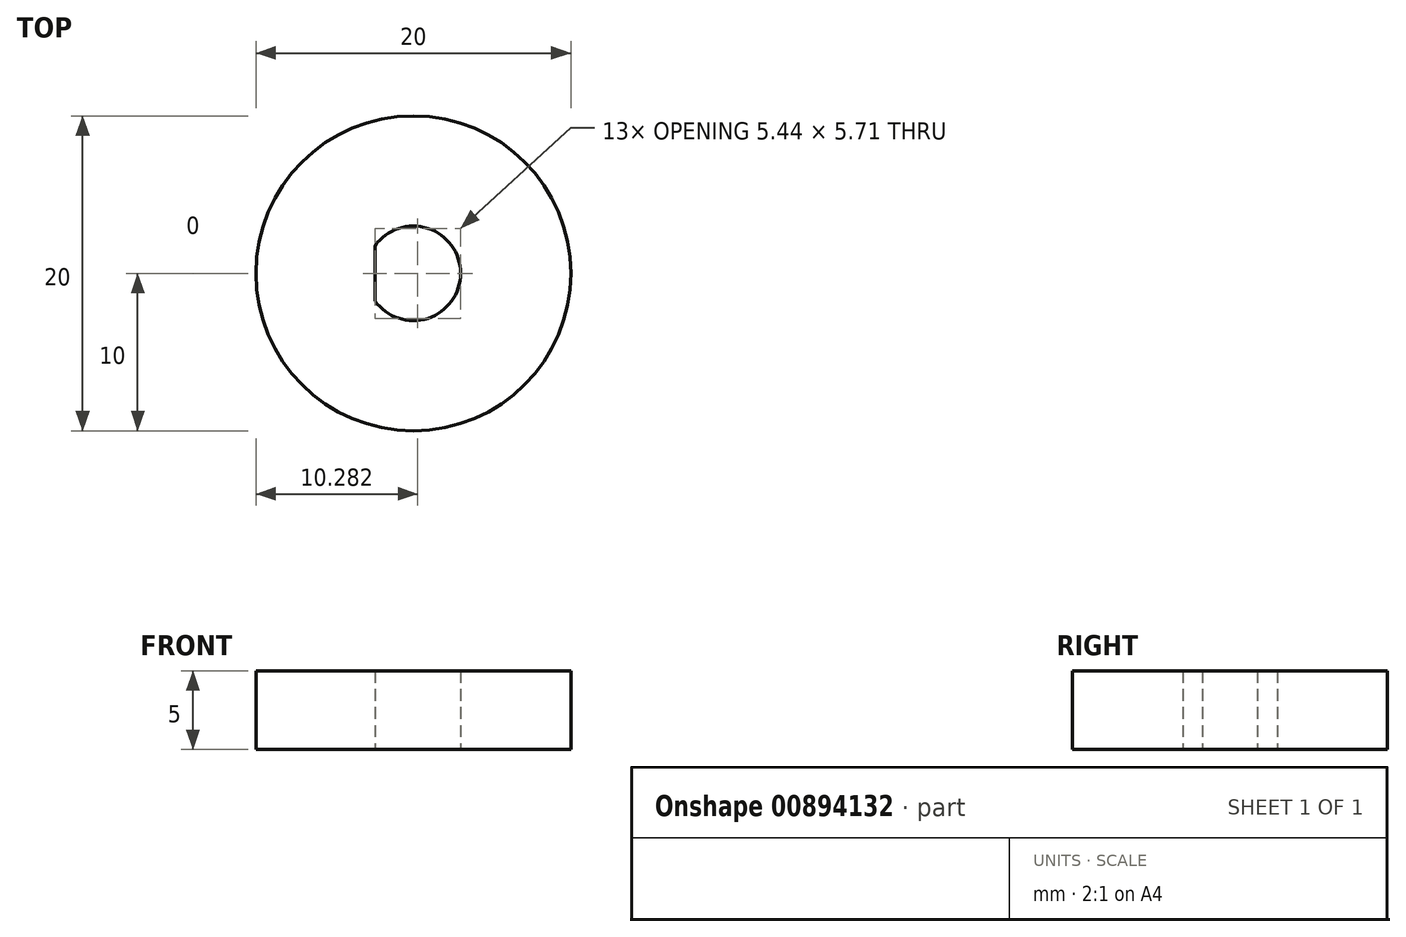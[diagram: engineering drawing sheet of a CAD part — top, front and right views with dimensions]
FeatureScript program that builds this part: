
annotation { "Feature Type Name" : "Feature", "Feature Type Description" : "" }
export const myFeature = defineFeature(function(context is Context, id is Id, definition is map)
    precondition{}
    {
        {
            var Q0;
            Q0=qCreatedBy(makeId("Top.planeOp"),FACE);
            var sketch = newSketch(context, id + "F0", { "sketchPlane" : qUnion([Q0])});
            skArc(sketch, "E0", {"start": v(-2.44, -1.75) * mm, "mid": v(3, 0) * mm, "end": v(-2.44, 1.75) * mm});
            skPoint(sketch, "E1.orphan", {"position": v(-2.44, 0.1) * mm});
            skPoint(sketch, "E2.start.orphan", {"position": v(3, 0) * mm});
            skLineSegment(sketch, "E3", {"start": v(-2.44, 1.75) * mm, "end": v(-2.44, -1.75) * mm});
            skSolve(sketch);
        }
        {
            var Q0;
            Q0=makeQuery(id+"F0.imprint","IMPRINT",FACE,{"disambiguationData":[TD([[makeQuery(id+"F0.imprint","IMPRINT",EDGE,{"derivedFrom":sQuery(id+"F0.wireOp",EDGE,"E0")}),1.0]])]});
            var sketch = newSketch(context, id + "F1", { "sketchPlane" : qUnion([Q0])});
            skCircle(sketch, "E4", {"center": v(0, 0) * mm, "radius": 10 * mm});
            skLineSegment(sketch, "E5", {"start": v(0, 0) * mm, "end": v(0, 10) * mm, "construction": true});
            skLineSegment(sketch, "E6", {"start": v(0, 0) * mm, "end": v(0, -10) * mm, "construction": true});
            skLineSegment(sketch, "E7", {"start": v(0, 0) * mm, "end": v(-10, 0) * mm, "construction": true});
            skLineSegment(sketch, "E8", {"start": v(0, 0) * mm, "end": v(10, 0) * mm, "construction": true});
            skSolve(sketch);
        }
        {
            var Q0;
            Q0=makeQuery(id+"F1.imprint","IMPRINT",FACE,{"disambiguationData":[TD([[makeQuery(id+"F1.imprint","IMPRINT",EDGE,{"derivedFrom":sQuery(id+"F1.wireOp",EDGE,"E4")}),1.0]])]});
            extrude(context, id + "F2", {"entities" : qUnion([Q0]), "depth" : 5 * mm, "offsetDistance" : 25 * mm});
        }
    });
